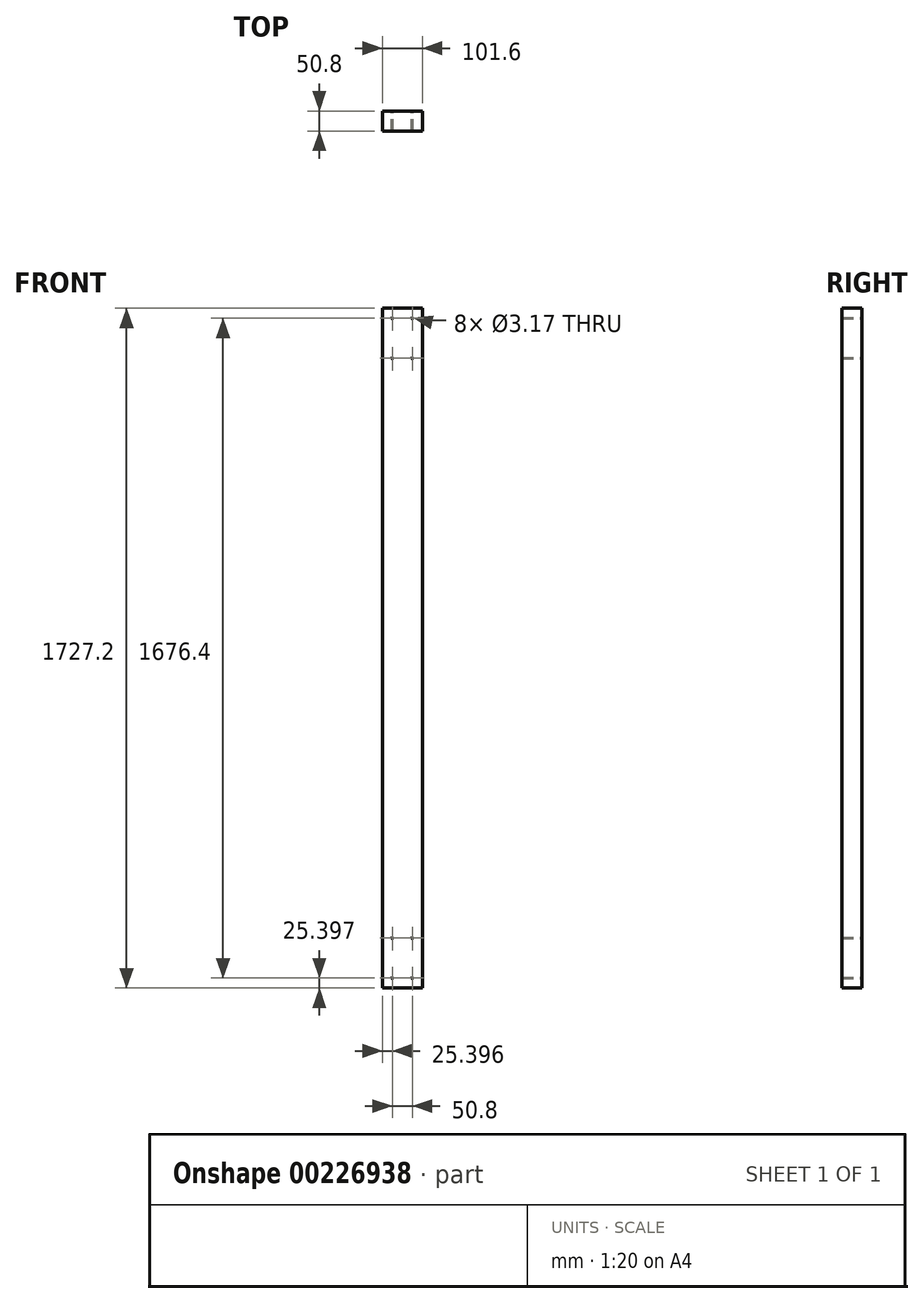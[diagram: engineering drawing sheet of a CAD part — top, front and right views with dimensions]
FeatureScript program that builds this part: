
annotation { "Feature Type Name" : "Feature", "Feature Type Description" : "" }
export const myFeature = defineFeature(function(context is Context, id is Id, definition is map)
    precondition{}
    {
        {
            var Q0;
            Q0=qCreatedBy(makeId("Front.planeOp"),FACE);
            var sketch = newSketch(context, id + "F0", { "sketchPlane" : qUnion([Q0])});
            skLineSegment(sketch, "E0.bottom", {"start": v(-90.6, 1453.8) * mm, "end": v(11, 1453.8) * mm});
            skLineSegment(sketch, "E0.top", {"start": v(-90.6, -273.4) * mm, "end": v(11, -273.4) * mm});
            skLineSegment(sketch, "E0.left", {"start": v(-90.6, 1453.8) * mm, "end": v(-90.6, -273.4) * mm});
            skLineSegment(sketch, "E0.right", {"start": v(11, 1453.8) * mm, "end": v(11, -273.4) * mm});
            skCircle(sketch, "E1", {"center": v(-65.2, 1428.4) * mm, "radius": 1.59 * mm});
            skCircle(sketch, "E2", {"center": v(-14.4, 1428.4) * mm, "radius": 1.59 * mm});
            skCircle(sketch, "E3", {"center": v(-65.2, 1326.8) * mm, "radius": 1.59 * mm});
            skCircle(sketch, "E4", {"center": v(-14.4, 1326.8) * mm, "radius": 1.59 * mm});
            skCircle(sketch, "E5", {"center": v(-14.4, -248) * mm, "radius": 1.59 * mm});
            skCircle(sketch, "E6", {"center": v(-65.2, -248) * mm, "radius": 1.59 * mm});
            skCircle(sketch, "E7", {"center": v(-65.2, -146.4) * mm, "radius": 1.59 * mm});
            skCircle(sketch, "E8", {"center": v(-14.4, -146.4) * mm, "radius": 1.59 * mm});
            skSolve(sketch);
        }
        {
            var Q0;
            Q0=makeQuery(id+"F0.imprint","IMPRINT",FACE,{"disambiguationData":[TD([[makeQuery(id+"F0.imprint","IMPRINT",EDGE,{"derivedFrom":sQuery(id+"F0.wireOp",EDGE,"E0.bottom")}),-1.0]])]});
            extrude(context, id + "F1", {"entities" : qUnion([Q0]), "depth" : 50.8 * mm});
        }
    });
